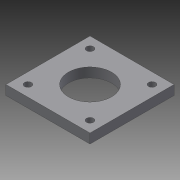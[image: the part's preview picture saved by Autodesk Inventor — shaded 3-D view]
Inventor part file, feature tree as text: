
AUTODESK INVENTOR PART (.ipt)
format: ipt  version: 2015 (Build 190159000, 159)  size: 89,088 bytes
history: native  units: in
note: dims shown in document units (in); Inventor stores cm internally (conversion verified against a paired STEP export)
features: extrude x1, sketch x1
ambient origin geometry x8: Origin, YZ Plane, XZ Plane, XY Plane, X Axis, Y Axis, Z Axis, Center Point
bodies: Body1 (feature_tree)
feature tree (2):
  extrude  "Extrusion4"  Depth=1.6535in
  sketch  "Sketch1"  dims[d0=1.6535in d1=1.6535in d4=0.1378in d8=0.8465in d11=0.1875in d12=0.0in d13=1.2205in]
